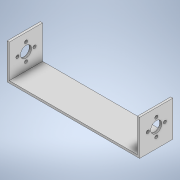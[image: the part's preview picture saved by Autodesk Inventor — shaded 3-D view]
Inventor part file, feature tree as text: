
AUTODESK INVENTOR PART (.ipt)
format: ipt  version: 2020 (Build 240168000, 168)  size: 132,608 bytes
history: native  units: in
note: dims shown in document units (in); Inventor stores cm internally (conversion verified against a paired STEP export)
features: extrude x3, sketch x3
ambient origin geometry x8: Origin, YZ Plane, XZ Plane, XY Plane, X Axis, Y Axis, Z Axis, Center Point
bodies: Solid1 (feature_tree)
feature tree (6):
  extrude  "Extrusion1"  Depth=1.5in
  sketch  "Sketch3"  dims[d2=0.1in d3=0.0in d7=0.77in]
  extrude  "Extrusion3"  Depth=0.1in
  extrude  "Extrusion4"  Depth=1.5in TaperAngle=0.0deg
  sketch  "Sketch1"  dims[d0=5.963in d1=1.5in]
  sketch  "Sketch4"  dims[d12=0.5in d13=1.5in d14=0.0in d15=8.0in d16=0.0in d17=0.1in]
